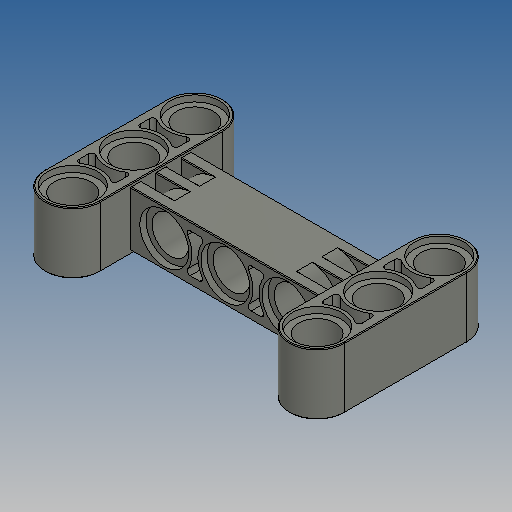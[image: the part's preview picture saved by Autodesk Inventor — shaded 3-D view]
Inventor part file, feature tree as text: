
AUTODESK INVENTOR PART (.ipt)
format: ipt  version: 2025 (Build 290162010, 162A)  size: 580,096 bytes
history: native  units: mm
features: extrude x8, sketch x5, mirror x4, fillet x3
ambient origin geometry x8: Origin, YZ Plane, XZ Plane, XY Plane, X Axis, Y Axis, Z Axis, Center Point
bodies: Solid1 (feature_tree)
feature tree (20):
  extrude  "Extrusion1"  Depth=0.8mm TaperAngle=0.0deg
  sketch  "Sketch6"  dims[d43=3.1mm d44=0.0mm d49=6.4mm]
  extrude  "Extrusion7"  Depth=6.4mm
  extrude  "Extrusion8"  Depth=0.1mm
  mirror  "Mirror5"
  fillet  "Fillet2"  Radius=0.1mm
  extrude  "Extrusion13"  Depth=8.0mm TaperAngle=0.0deg
  sketch  "Sketch12"  dims[d64=8.0mm d90=8.0mm d91=0.0mm]
  extrude  "Extrusion14"  Depth=0.1mm TaperAngle=0.0deg
  extrude  "Extrusion15"  Depth=0.1mm TaperAngle=0.0deg
  extrude  "Extrusion16"  TaperAngle=45.0deg  [1 undecoded]
  extrude  "Extrusion20"  Depth=0.1mm
  fillet  "Fillet4"  Radius=7.2mm
  mirror  "Mirror6"
  mirror  "Mirror4"
  mirror  "Mirror3"
  fillet  "Fillet5"  Radius=2.222mm
  sketch  "Sketch1"  dims[d14=8.0mm d15=0.0mm d41=0.8mm d42=0.0mm]
  sketch  "Sketch11"  dims[d50=4.8mm d51=8.0mm d60=0.4mm d61=0.1mm]
  sketch  "Sketch16"  dims[d94=0.9mm d95=0.0mm d96=3.2mm d97=0.0mm d98=0.8mm d99=0.0mm d116=45.0deg d119=7.2mm d121=7.2mm d123=2.222mm d124=4.8mm d125=6.4mm d126=45.0deg d127=1.4mm d128=10.0mm d129=0.0mm d130=0.4mm d131=16.0mm d132=16.0mm d133=0.1mm]
note: 1 required parameter value undecoded (feature->parameter linkage not recoverable at this tier; creation-order binding heuristic only, values carry confidence <= 0.55)
